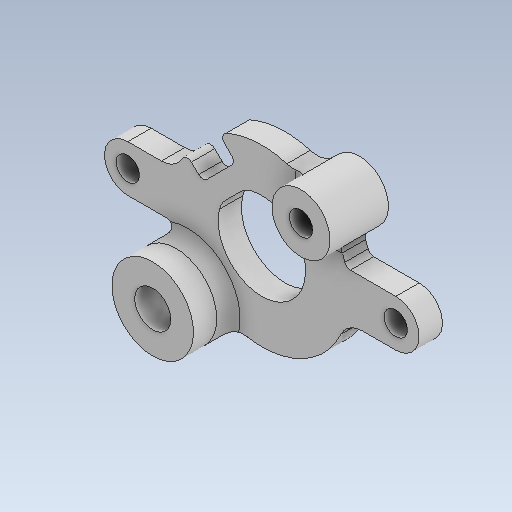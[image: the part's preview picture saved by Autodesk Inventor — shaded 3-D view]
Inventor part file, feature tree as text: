
AUTODESK INVENTOR PART (.ipt)
format: ipt  version: 2020 (Build 240168000, 168)  size: 408,064 bytes
history: native  units: mm
features: fillet x6, extrude x5, sketch x5, reference x5, projected_geometry x5, other x5, chamfer x1
ambient origin geometry x8: Origin, YZ Plane, XZ Plane, XY Plane, X Axis, Y Axis, Z Axis, Center Point
bodies: Solid1 (feature_tree)
feature tree (32):
  extrude  "Extrusion1"  Depth=4.0mm
  extrude  "Extrusion2"  Depth=4.0mm
  fillet  "Fillet1"  Radius=7.5mm
  fillet  "Fillet2"  Radius=9.0mm
  fillet  "Fillet3"  Radius=9.0mm
  fillet  "Fillet4"  Radius=15.0mm
  extrude  "Extrusion3"  Depth=7.0mm
  fillet  "Fillet5"  Radius=4.0mm
  extrude  "Extrusion4"  Depth=7.0mm
  extrude  "Extrusion5"  Depth=2.0mm TaperAngle=0.0deg
  chamfer  "Chamfer1"  Distance=0.5mm
  fillet  "Fillet6"  Radius=2.0mm
  sketch  "Sketch1"  dims[d0=4.0mm d1=4.0mm]
  reference  "Reference1"
  reference  "Reference2"
  reference  "Reference3"
  reference  "Reference4"
  sketch  "Sketch2"  dims[d2=4.8mm d3=4.0mm d4=7.5mm d5=9.0mm d6=9.0mm d7=15.0mm]
  projected_geometry  "Projected Loop1"
  reference  "Reference5"
  sketch  "Sketch3"  dims[d8=5.0mm d9=7.0mm d10=4.0mm]
  projected_geometry  "Projected Loop2"
  sketch  "Sketch4"  dims[d11=5.0mm d12=7.0mm]
  projected_geometry  "Projected Loop3"
  projected_geometry  "Projected Loop4"
  sketch  "Sketch5"  dims[d13=2.0mm d14=0.0mm d15=2.0mm d16=0.0mm d17=0.5mm d18=2.0mm d19=2.0mm d20=0.5mm d21=5.0mm d22=7.0mm d23=3.0mm d24=0.0mm d25=1.0mm d26=3.1mm d27=2.0mm d28=3.0mm d29=0.0mm d30=1.0mm d31=0.0mm d32=1.0mm d33=2.0mm d34=45.0deg d35=1.0mm]
  projected_geometry  "Projected Loop5"
  parser-record x1  (decoder bookkeeping rows leaked as tree rows — omitted from the tree; the rows remain in map.json)
  other  "reducer_1.iam"
  other  "mot_holder_1:1"
  other  "mot_27_ass:1"
  other  "mot_27_2:1"
note: 1 file-system path scrubbed to <path> (originals preserved in map.json)
